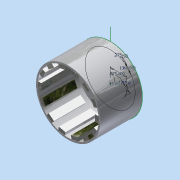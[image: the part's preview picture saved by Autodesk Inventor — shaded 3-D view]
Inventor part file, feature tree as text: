
AUTODESK INVENTOR PART (.ipt)
format: ipt  version: 2015 (Build 190159000, 159)  size: 344,064 bytes
history: native  units: in
note: dims shown in document units (in); Inventor stores cm internally (conversion verified against a paired STEP export)
features: other x4, sketch x3, revolve x1, plane x1, extrude x1, pattern_circular x1, projected_geometry x1
ambient origin geometry x8: Origin, YZ Plane, XZ Plane, XY Plane, X Axis, Y Axis, Z Axis, Center Point
bodies: Solid1 (feature_tree), Solid2 (feature_tree)
feature tree (12):
  other  "Stator.ipt"
  revolve  "Revolution1"  [1 undecoded]
  plane  "Work Plane1"
  extrude  "Extrusion1"  Depth=0.0625in
  pattern_circular  "Circular Pattern1"  [2 undecoded]
  sketch  "Sketch3"  dims[d4=0.125in d5=0.0625in d6=0.25in d7=0.0625in d8=90.0deg d9=0.125in d10=0.25in d11=1.0in d12=0.0in d13=5.5118in d14=360.0deg d16=0.25in d17=0.375in d18=0.6in d19=1.5748in d21=360.0deg d23=0.375in d24=45.0deg d25=0.25in d26=1.5748in d28=360.0deg]
  other  "TaggingFeature1"
  sketch  "Sketch1"  dims[d0=0.3937in d1=0.2953in]
  sketch  "Sketch2"  dims[d2=0.1447in d3=0.0625in]
  projected_geometry  "Projected Loop2"
  other  "Solid1::Stator.ipt"
  other  "Srf1"
note: 3 required parameter values undecoded (feature->parameter linkage not recoverable at this tier; creation-order binding heuristic only, values carry confidence <= 0.55)